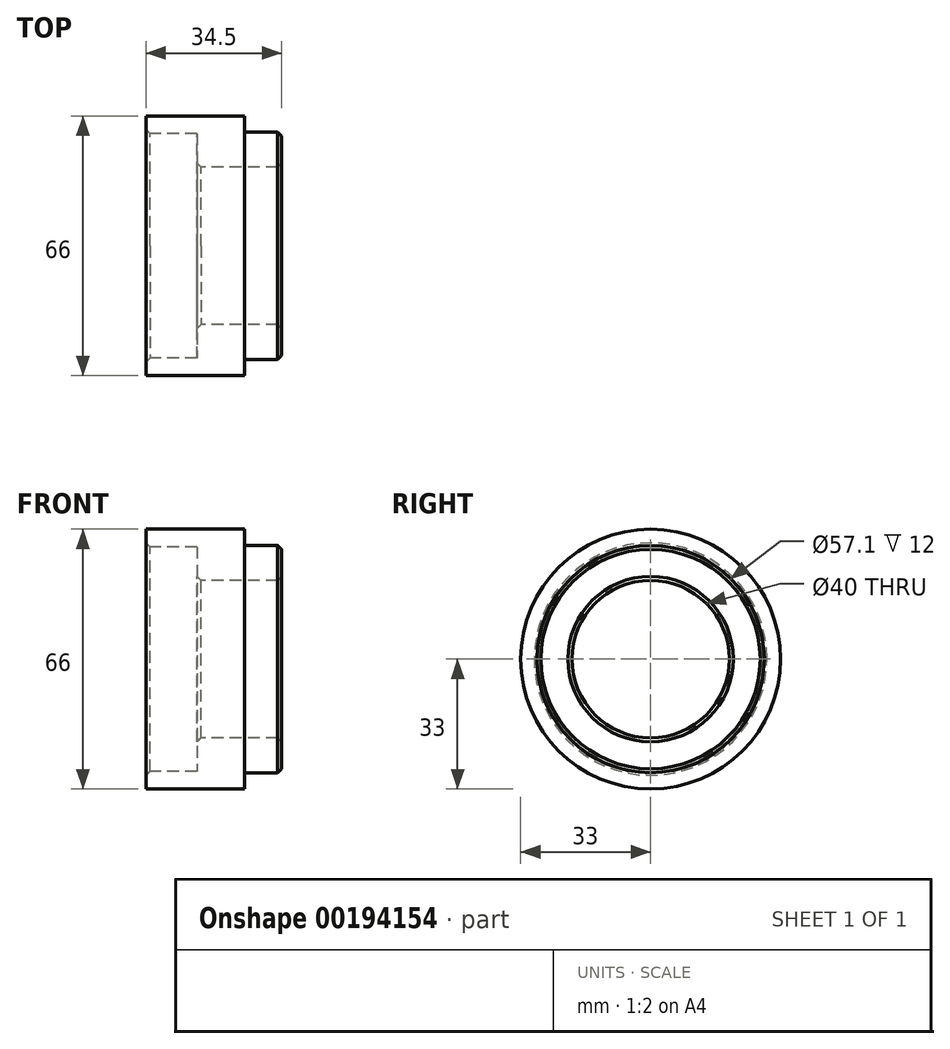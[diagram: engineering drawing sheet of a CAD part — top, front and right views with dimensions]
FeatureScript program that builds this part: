
annotation { "Feature Type Name" : "Feature", "Feature Type Description" : "" }
export const myFeature = defineFeature(function(context is Context, id is Id, definition is map)
    precondition{}
    {
        {
            var Q0;
            Q0=qCreatedBy(makeId("Front.planeOp"),FACE);
            var sketch = newSketch(context, id + "F0", { "sketchPlane" : qUnion([Q0])});
            skLineSegment(sketch, "E0", {"start": v(-159.38, 0) * mm, "end": v(166.26, 0) * mm, "construction": true});
            skLineSegment(sketch, "E1", {"start": v(0, -95.28) * mm, "end": v(0, 96.66) * mm, "construction": true});
            skLineSegment(sketch, "E2.bottom", {"start": v(0, 33) * mm, "end": v(25, 33) * mm});
            skLineSegment(sketch, "E2.top", {"start": v(0, 28.55) * mm, "end": v(13, 28.55) * mm});
            skLineSegment(sketch, "E2.left", {"start": v(0, 33) * mm, "end": v(0, 28.55) * mm});
            skLineSegment(sketch, "E3.top", {"start": v(13, 20) * mm, "end": v(34.5, 20) * mm});
            skLineSegment(sketch, "E3.left", {"start": v(13, 28.55) * mm, "end": v(13, 20) * mm});
            skLineSegment(sketch, "E4", {"start": v(34.5, 20) * mm, "end": v(34.5, 28.86) * mm});
            skLineSegment(sketch, "E5.top", {"start": v(25, 28.86) * mm, "end": v(34.5, 28.86) * mm});
            skLineSegment(sketch, "E5.left", {"start": v(25, 33) * mm, "end": v(25, 28.86) * mm});
            skSolve(sketch);
        }
        {
            var Q0;
            Q0 = qSketchRegion(id + "F0", true);
            var Q1;
            Q1=sQuery(id+"F0.wireOp",EDGE,"E0");
            revolve(context, id + "F1", {"entities" : qUnion([Q0]), "axis" : qUnion([Q1]), "revolveType" : RevolveType.FULL});
        }
        {
            var Q0;
            Q0=makeQuery(id+"F1.opRevolve","SWEPT_EDGE",EDGE,{"disambiguationData":[OSD([sQuery(id+"F0.wireOp",EDGE,"E2.top"),sQuery(id+"F0.wireOp",EDGE,"E2.left")])]});
            var Q1;
            Q1=makeQuery(id+"F1.opRevolve","SWEPT_EDGE",EDGE,{"disambiguationData":[OSD([sQuery(id+"F0.wireOp",EDGE,"E3.top"),sQuery(id+"F0.wireOp",EDGE,"E4")])]});
            var Q2;
            Q2=makeQuery(id+"F1.opRevolve","SWEPT_FACE",FACE,{"disambiguationData":[OSD([sQuery(id+"F0.wireOp",EDGE,"E4")])]});
            var Q3;
            Q3=makeQuery(id+"F1.opRevolve","SWEPT_EDGE",EDGE,{"disambiguationData":[OSD([sQuery(id+"F0.wireOp",EDGE,"E3.top"),sQuery(id+"F0.wireOp",EDGE,"E3.left")])]});
            chamfer(context, id + "F2", {"entities" : qUnion([Q0, Q1, Q2, Q3]), "width" : 1 * mm, "tangentPropagation" : true});
        }
    });
